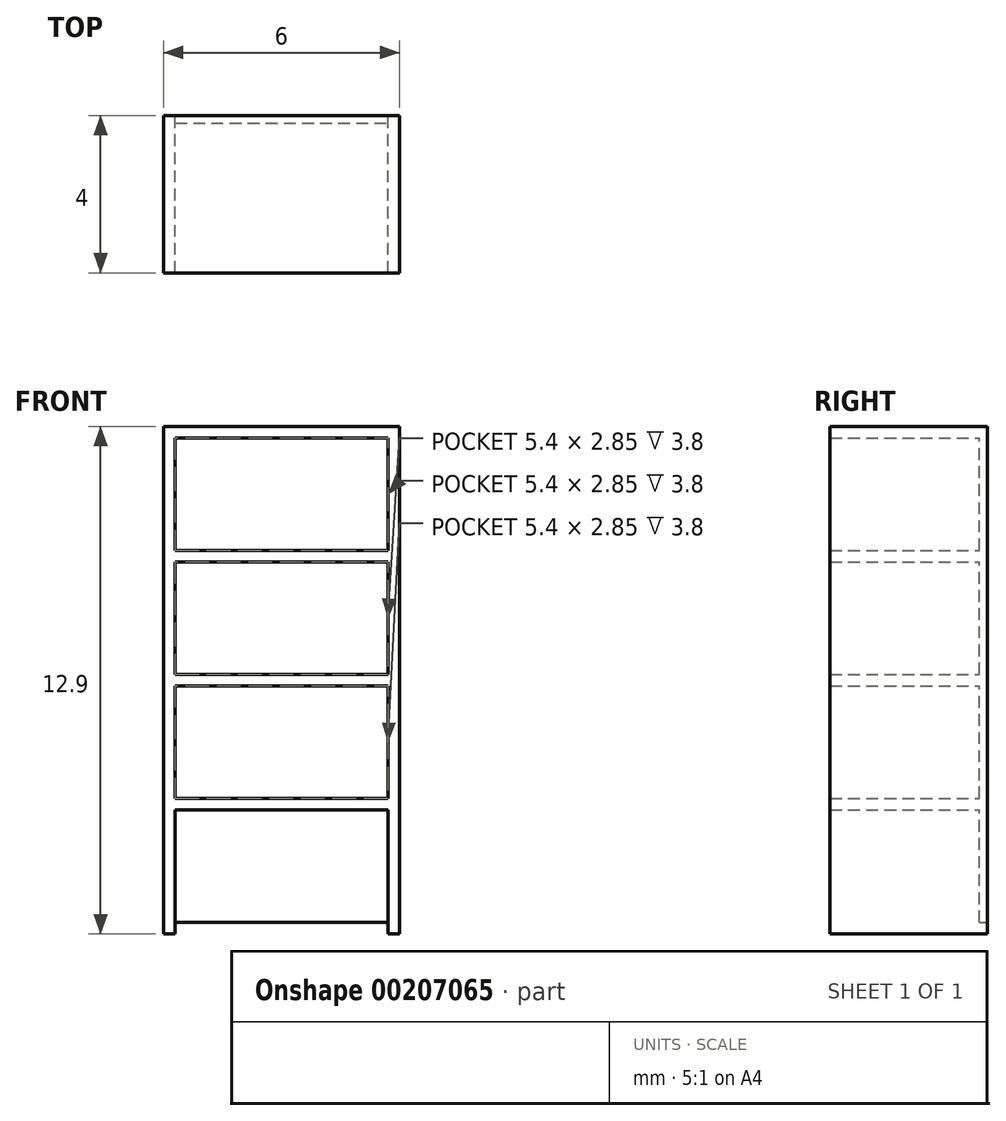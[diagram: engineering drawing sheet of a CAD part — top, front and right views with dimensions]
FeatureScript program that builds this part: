
annotation { "Feature Type Name" : "Feature", "Feature Type Description" : "" }
export const myFeature = defineFeature(function(context is Context, id is Id, definition is map)
    precondition{}
    {
        {
            var Q0;
            Q0=qCreatedBy(makeId("Front.planeOp"),FACE);
            var sketch = newSketch(context, id + "F0", { "sketchPlane" : qUnion([Q0])});
            skLineSegment(sketch, "E0.bottom", {"start": v(-3, 0) * mm, "end": v(3, 0) * mm});
            skLineSegment(sketch, "E0.top", {"start": v(-3, 12.9) * mm, "end": v(3, 12.9) * mm});
            skLineSegment(sketch, "E0.left", {"start": v(-3, 0) * mm, "end": v(-3, 12.9) * mm});
            skLineSegment(sketch, "E0.right", {"start": v(3, 0) * mm, "end": v(3, 12.9) * mm});
            skLineSegment(sketch, "E1.bottom", {"start": v(-2.7, 0) * mm, "end": v(2.7, 0) * mm});
            skLineSegment(sketch, "E1.top", {"start": v(-2.7, 12.9) * mm, "end": v(2.7, 12.9) * mm});
            skLineSegment(sketch, "E1.left", {"start": v(-2.7, 0) * mm, "end": v(-2.7, 12.9) * mm});
            skLineSegment(sketch, "E1.right", {"start": v(2.7, 0) * mm, "end": v(2.7, 12.9) * mm});
            skLineSegment(sketch, "E2", {"start": v(-2.7, 6.45) * mm, "end": v(-3, 6.45) * mm, "construction": true});
            skLineSegment(sketch, "E3", {"start": v(2.7, 6.45) * mm, "end": v(3, 6.45) * mm, "construction": true});
            skLineSegment(sketch, "E4.top", {"start": v(-2.7, 0.3) * mm, "end": v(2.7, 0.3) * mm});
            skLineSegment(sketch, "E4.left", {"start": v(-2.7, 0) * mm, "end": v(-2.7, 0.3) * mm});
            skLineSegment(sketch, "E4.right", {"start": v(2.7, 0) * mm, "end": v(2.7, 0.3) * mm});
            skLineSegment(sketch, "E5.bottom", {"start": v(-2.7, 6.3) * mm, "end": v(2.7, 6.3) * mm});
            skLineSegment(sketch, "E5.top", {"start": v(-2.7, 6.6) * mm, "end": v(2.7, 6.6) * mm});
            skLineSegment(sketch, "E5.left", {"start": v(-2.7, 6.3) * mm, "end": v(-2.7, 6.6) * mm});
            skLineSegment(sketch, "E5.right", {"start": v(2.7, 6.3) * mm, "end": v(2.7, 6.6) * mm});
            skLineSegment(sketch, "E6.bottom", {"start": v(-2.7, 9.45) * mm, "end": v(2.7, 9.45) * mm});
            skLineSegment(sketch, "E6.top", {"start": v(-2.7, 9.75) * mm, "end": v(2.7, 9.75) * mm});
            skLineSegment(sketch, "E6.left", {"start": v(-2.7, 9.45) * mm, "end": v(-2.7, 9.75) * mm});
            skLineSegment(sketch, "E6.right", {"start": v(2.7, 9.45) * mm, "end": v(2.7, 9.75) * mm});
            skLineSegment(sketch, "E7.bottom", {"start": v(-2.7, 12.6) * mm, "end": v(2.7, 12.6) * mm});
            skLineSegment(sketch, "E7.left", {"start": v(-2.7, 12.6) * mm, "end": v(-2.7, 12.9) * mm});
            skLineSegment(sketch, "E7.right", {"start": v(2.7, 12.6) * mm, "end": v(2.7, 12.9) * mm});
            skLineSegment(sketch, "E8.bottom", {"start": v(-2.7, 3.45) * mm, "end": v(2.7, 3.45) * mm});
            skLineSegment(sketch, "E8.top", {"start": v(-2.7, 3.15) * mm, "end": v(2.7, 3.15) * mm});
            skLineSegment(sketch, "E8.left", {"start": v(-2.7, 3.45) * mm, "end": v(-2.7, 3.15) * mm});
            skLineSegment(sketch, "E8.right", {"start": v(2.7, 3.45) * mm, "end": v(2.7, 3.15) * mm});
            skLineSegment(sketch, "E9", {"start": v(0, 9.75) * mm, "end": v(0, 12.6) * mm, "construction": true});
            skLineSegment(sketch, "E10", {"start": v(0, 9.45) * mm, "end": v(0, 6.6) * mm, "construction": true});
            skLineSegment(sketch, "E11", {"start": v(0, 6.3) * mm, "end": v(0, 3.45) * mm, "construction": true});
            skLineSegment(sketch, "E12", {"start": v(0, 3.15) * mm, "end": v(0, 0.3) * mm, "construction": true});
            skSolve(sketch);
        }
        {
            var Q0;
            {var subQ7=sQuery(id+"F0.wireOp",EDGE,"E0.left");Q0=makeQuery(id+"F0.imprint","IMPRINT",FACE,{"disambiguationData":[TD([[makeQuery(id+"F0.imprint","IMPRINT",EDGE,{"derivedFrom":subQ7}),-1.0]])]});}
            var Q1;
            {var subQ5=sQuery(id+"F0.wireOp",EDGE,"E0.right");Q1=makeQuery(id+"F0.imprint","IMPRINT",FACE,{"disambiguationData":[TD([[makeQuery(id+"F0.imprint","IMPRINT",EDGE,{"derivedFrom":subQ5}),1.0]])]});}
            var Q2;
            Q2=makeQuery(id+"F0.imprint","IMPRINT",FACE,{"disambiguationData":[TD([[makeQuery(id+"F0.imprint","IMPRINT",EDGE,{"derivedFrom":sQuery(id+"F0.wireOp",EDGE,"E7.bottom")}),1.0]])]});
            var Q3;
            Q3=makeQuery(id+"F0.imprint","IMPRINT",FACE,{"disambiguationData":[TD([[makeQuery(id+"F0.imprint","IMPRINT",EDGE,{"derivedFrom":sQuery(id+"F0.wireOp",EDGE,"E6.bottom")}),1.0]])]});
            var Q4;
            Q4=makeQuery(id+"F0.imprint","IMPRINT",FACE,{"disambiguationData":[TD([[makeQuery(id+"F0.imprint","IMPRINT",EDGE,{"derivedFrom":sQuery(id+"F0.wireOp",EDGE,"E5.bottom")}),1.0]])]});
            var Q5;
            Q5=makeQuery(id+"F0.imprint","IMPRINT",FACE,{"disambiguationData":[TD([[makeQuery(id+"F0.imprint","IMPRINT",EDGE,{"derivedFrom":sQuery(id+"F0.wireOp",EDGE,"E8.bottom")}),-1.0]])]});
            var Q6;
            Q6=makeQuery(id+"F0.imprint","IMPRINT",FACE,{"disambiguationData":[TD([[makeQuery(id+"F0.imprint","IMPRINT",EDGE,{"derivedFrom":sQuery(id+"F0.wireOp",EDGE,"E1.bottom")}),1.0]])]});
            extrude(context, id + "F1", {"entities" : qUnion([Q0, Q1, Q2, Q3, Q4, Q5, Q6]), "depth" : 4 * mm});
        }
        {
            var Q0;
            {var subQ0=sQuery(id+"F0.wireOp",EDGE,"E6.top");Q0=makeQuery(id+"F0.imprint","IMPRINT",FACE,{"disambiguationData":[TD([[makeQuery(id+"F0.imprint","IMPRINT",EDGE,{"derivedFrom":subQ0}),1.0]])]});}
            var Q1;
            {var subQ0=sQuery(id+"F0.wireOp",EDGE,"E5.bottom");Q1=makeQuery(id+"F0.imprint","IMPRINT",FACE,{"disambiguationData":[TD([[makeQuery(id+"F0.imprint","IMPRINT",EDGE,{"derivedFrom":subQ0}),-1.0]])]});}
            var Q2;
            {var subQ0=sQuery(id+"F0.wireOp",EDGE,"E4.top");Q2=makeQuery(id+"F0.imprint","IMPRINT",FACE,{"disambiguationData":[TD([[makeQuery(id+"F0.imprint","IMPRINT",EDGE,{"derivedFrom":subQ0}),1.0]])]});}
            var Q3;
            {var subQ0=sQuery(id+"F0.wireOp",EDGE,"E5.top");Q3=makeQuery(id+"F0.imprint","IMPRINT",FACE,{"disambiguationData":[TD([[makeQuery(id+"F0.imprint","IMPRINT",EDGE,{"derivedFrom":subQ0}),1.0]])]});}
            extrude(context, id + "F2", {"entities" : qUnion([Q0, Q1, Q2, Q3]), "operationType" : NewBodyOperationType.ADD, "depth" : 0.2 * mm});
        }
    });
